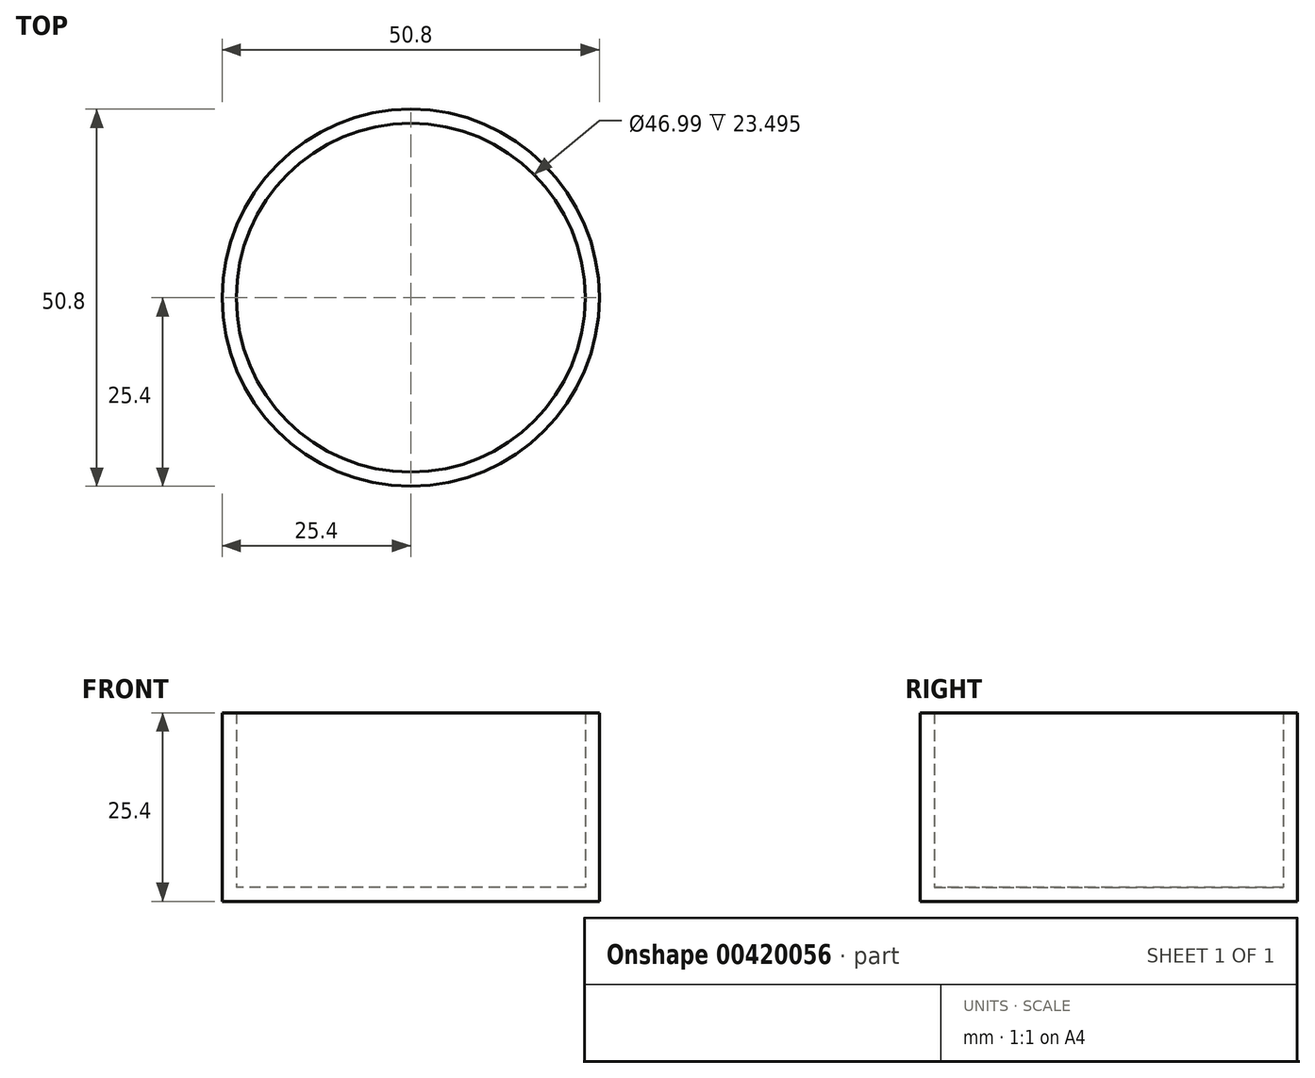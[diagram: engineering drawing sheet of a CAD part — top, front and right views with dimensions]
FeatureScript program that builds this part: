
annotation { "Feature Type Name" : "Feature", "Feature Type Description" : "" }
export const myFeature = defineFeature(function(context is Context, id is Id, definition is map)
    precondition{}
    {
        {
            var Q0;
            Q0=qCreatedBy(makeId("Top.planeOp"),FACE);
            var sketch = newSketch(context, id + "F0", { "sketchPlane" : qUnion([Q0])});
            skCircle(sketch, "E0", {"center": v(0, 0) * mm, "radius": 25.4 * mm});
            skSolve(sketch);
        }
        {
            var Q0;
            Q0 = qSketchRegion(id + "F0", true);
            extrude(context, id + "F1", {"entities" : qUnion([Q0]), "depth" : 25.4 * mm});
        }
        {
            var Q0;
            Q0=qCreatedBy(makeId("Top.planeOp"),FACE);
            var sketch = newSketch(context, id + "F2", { "sketchPlane" : qUnion([Q0])});
            skCircle(sketch, "E1.0", {"center": v(0, 0) * mm, "radius": 24.13 * mm});
            skSolve(sketch);
        }
        {
            var Q0;
            Q0=sQuery(id+"F2.wireOp",EDGE,"E1.0");
            extrude(context, id + "F3", {"bodyType" : ToolBodyType.SURFACE, "surfaceEntities" : qUnion([Q0]), "depth" : 6.35 * mm});
        }
        {
            var Q0;
            Q0=makeQuery(id+"F1.opExtrude","CAP_FACE",FACE,{"disambiguationData":[OSD([sQuery(id+"F0.wireOp",EDGE,"E0")])],"isStart":false});
            shell(context, id + "F4", {"entities" : qUnion([Q0]), "thickness" : 1.9 * mm});
        }
    });
